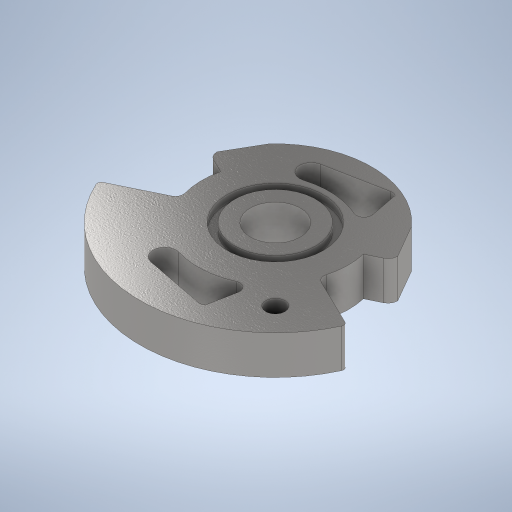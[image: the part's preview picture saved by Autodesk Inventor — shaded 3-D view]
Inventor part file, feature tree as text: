
AUTODESK INVENTOR PART (.ipt)
format: ipt  version: 2024 (Build 280153000, 153)  size: 401,408 bytes
history: native  units: mm
features: sketch x6, extrude x5, fillet x3, plane x2, mirror x2, hole x1
ambient origin geometry x8: Origin, YZ Plane, XZ Plane, XY Plane, X Axis, Y Axis, Z Axis, Center Point
bodies: Volumenkörper1 (feature_tree)
feature tree (19):
  extrude  "Extrusion1"  Depth=38.0mm
  fillet  "Rundung1"  Radius=4.537856mm
  hole  "Bohrung1"  [1 undecoded]
  fillet  "Rundung2"  Radius=9.075712mm
  fillet  "Rundung3"  Radius=48.0mm
  extrude  "Extrusion2"  Depth=60.0mm
  plane  "Arbeitsebene1"
  mirror  "Spiegeln1"
  extrude  "Extrusion3"  Depth=10.0mm TaperAngle=0.0deg
  extrude  "Extrusion4"  TaperAngle=45.0deg  [1 undecoded]
  extrude  "Extrusion5"  Depth=1.0mm
  plane  "Arbeitsebene2"
  mirror  "Spiegeln2"
  sketch  "Skizze1"  dims[d0=64.4mm d3=38.0mm d4=4.537856mm]
  sketch  "Skizze2"  dims[d5=9.075712mm d6=4.537856mm d7=9.075712mm d8=48.0mm]
  sketch  "Skizze3"  dims[d9=64.4mm d10=60.0mm]
  sketch  "Skizze4"  dims[d11=25.0mm d12=10.0mm d13=0.0mm]
  sketch  "Skizze5"  dims[d14=2.5mm d15=45.0deg]
  sketch  "Skizze6"  dims[d16=26.5mm d17=5.0mm d18=6.0mm d19=4.0mm d20=2.0mm d21=90.0deg d22=8.0mm d23=20.594885mm d24=1.0mm d25=2.0mm d27=30.0deg d28=0.0mm d29=0.0mm d30=0.0mm d31=13.0mm d32=10.0mm d33=0.0mm d34=21.0mm d35=25.0mm d36=2.0mm d37=0.0mm d38=15.0mm d40=6.0mm d41=3.0mm d42=19.995873mm d43=22.0mm d44=26.0mm d45=20.03364mm d46=2.0mm d47=0.0mm d48=-3.0mm]
note: 2 required parameter values undecoded (feature->parameter linkage not recoverable at this tier; creation-order binding heuristic only, values carry confidence <= 0.55)
